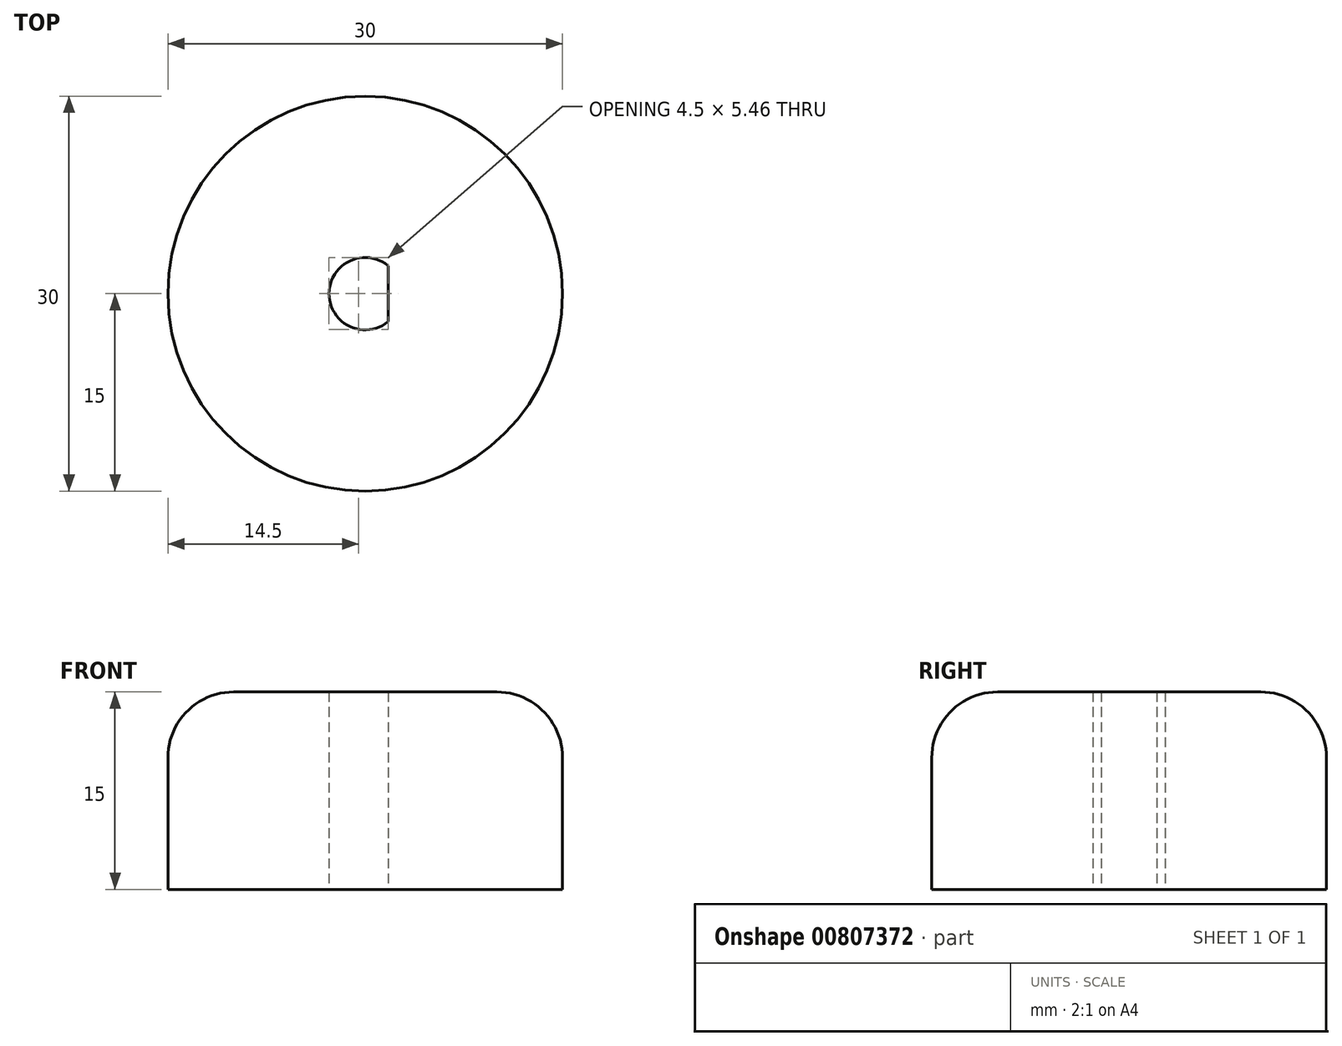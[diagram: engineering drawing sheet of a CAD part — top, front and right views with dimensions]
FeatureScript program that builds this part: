
annotation { "Feature Type Name" : "Feature", "Feature Type Description" : "" }
export const myFeature = defineFeature(function(context is Context, id is Id, definition is map)
    precondition{}
    {
        {
            var Q0;
            Q0=qCreatedBy(makeId("Top.planeOp"),FACE);
            var sketch = newSketch(context, id + "F0", { "sketchPlane" : qUnion([Q0])});
            skCircle(sketch, "E0", {"center": v(0, 0) * mm, "radius": 15 * mm});
            skSolve(sketch);
        }
        {
            var Q0;
            Q0=qSketchRegion(id+"F0",true);
            extrude(context, id + "F1", {"entities" : qUnion([Q0]), "depth" : 15 * mm});
        }
        {
            var Q0;
            Q0=makeQuery(id+"F1.opExtrude","CAP_FACE",FACE,{"disambiguationData":[OSD([sQuery(id+"F0.wireOp",EDGE,"E0")])],"isStart":true});
            var sketch = newSketch(context, id + "F2", { "sketchPlane" : qUnion([Q0])});
            skArc(sketch, "E1", {"start": v(1.75, 2.12) * mm, "mid": v(-2.75, 0) * mm, "end": v(1.75, -2.12) * mm});
            skLineSegment(sketch, "E2", {"start": v(1.75, 2.12) * mm, "end": v(1.75, -2.12) * mm});
            skPoint(sketch, "E3.orphan", {"position": v(1.75, 3.72) * mm});
            skPoint(sketch, "E4.orphan", {"position": v(-2.75, 0) * mm});
            skPoint(sketch, "E5.end.orphan", {"position": v(1.75, 0) * mm});
            skSolve(sketch);
        }
        {
            var Q0;
            Q0=qSketchRegion(id+"F2",true);
            extrude(context, id + "F3", {"entities" : qUnion([Q0]), "operationType" : NewBodyOperationType.REMOVE, "oppositeDirection" : true, "depth" : 25 * mm});
        }
        {
            var Q0;
            Q0=makeQuery(id+"F1.opExtrude","CAP_EDGE",EDGE,{"disambiguationData":[OSD([sQuery(id+"F0.wireOp",EDGE,"E0")])],"isStart":false});
            fillet(context, id + "F4", {"entities" : qUnion([Q0]), "radius" : 5 * mm, "tangentPropagation" : true, "allowEdgeOverflow" : false});
        }
    });
